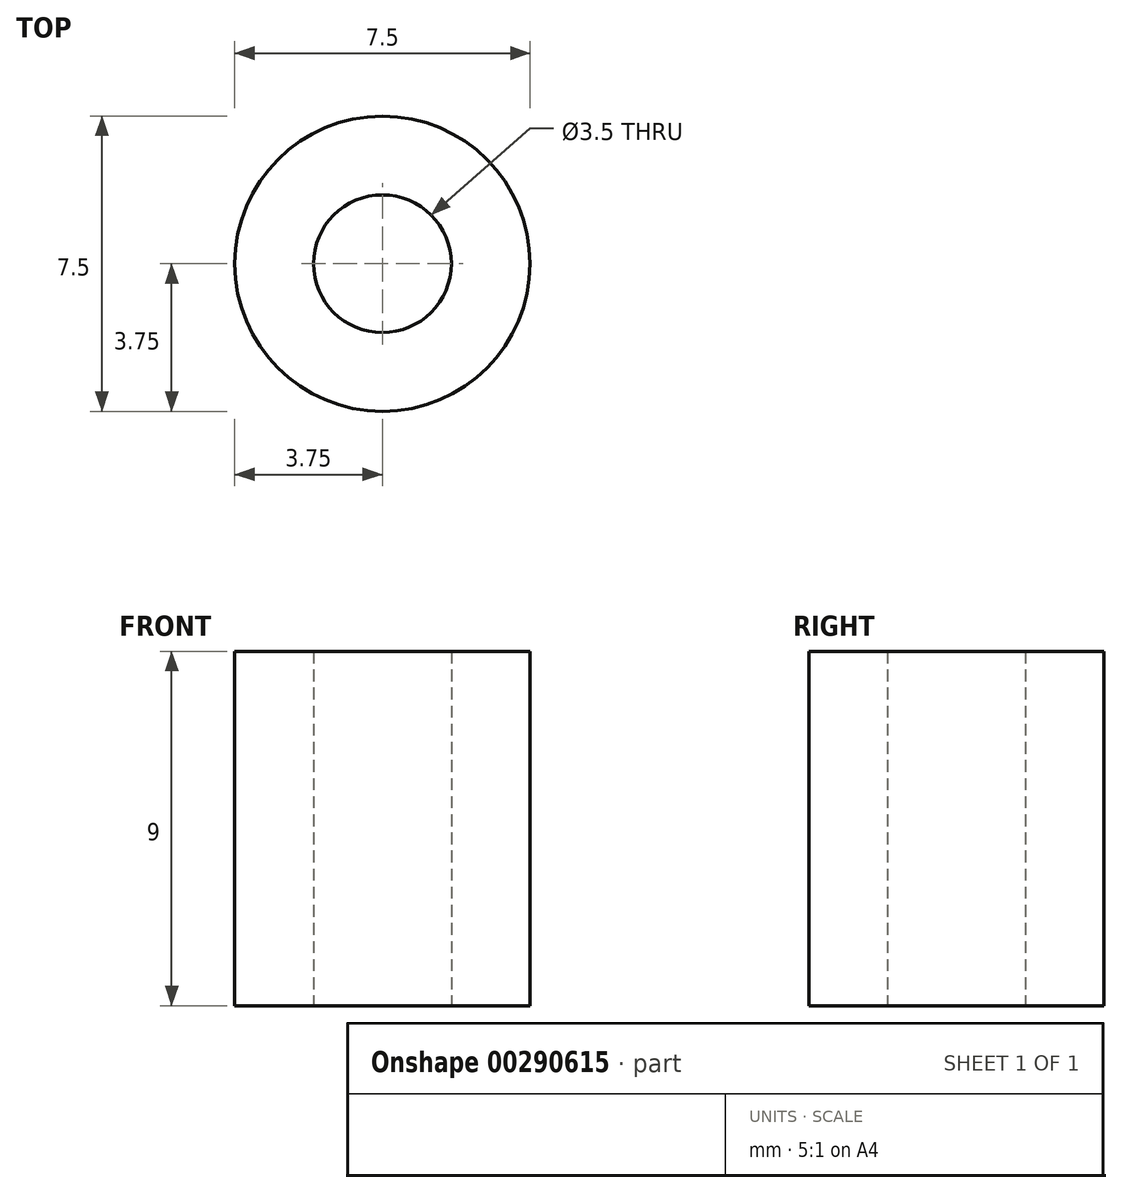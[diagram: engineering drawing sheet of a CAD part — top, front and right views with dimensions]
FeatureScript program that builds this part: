
annotation { "Feature Type Name" : "Feature", "Feature Type Description" : "" }
export const myFeature = defineFeature(function(context is Context, id is Id, definition is map)
    precondition{}
    {
        {
            var Q0;
            Q0=qCreatedBy(makeId("Top.planeOp"),FACE);
            var sketch = newSketch(context, id + "F0", { "sketchPlane" : qUnion([Q0])});
            skCircle(sketch, "E0", {"center": v(0, 0) * mm, "radius": 1.75 * mm});
            skCircle(sketch, "E1", {"center": v(0, 0) * mm, "radius": 3.75 * mm});
            skSolve(sketch);
        }
        {
            var Q0;
            Q0 = qSketchRegion(id + "F0", true);
            extrude(context, id + "F1", {"entities" : qUnion([Q0]), "depth" : 9 * mm});
        }
    });
